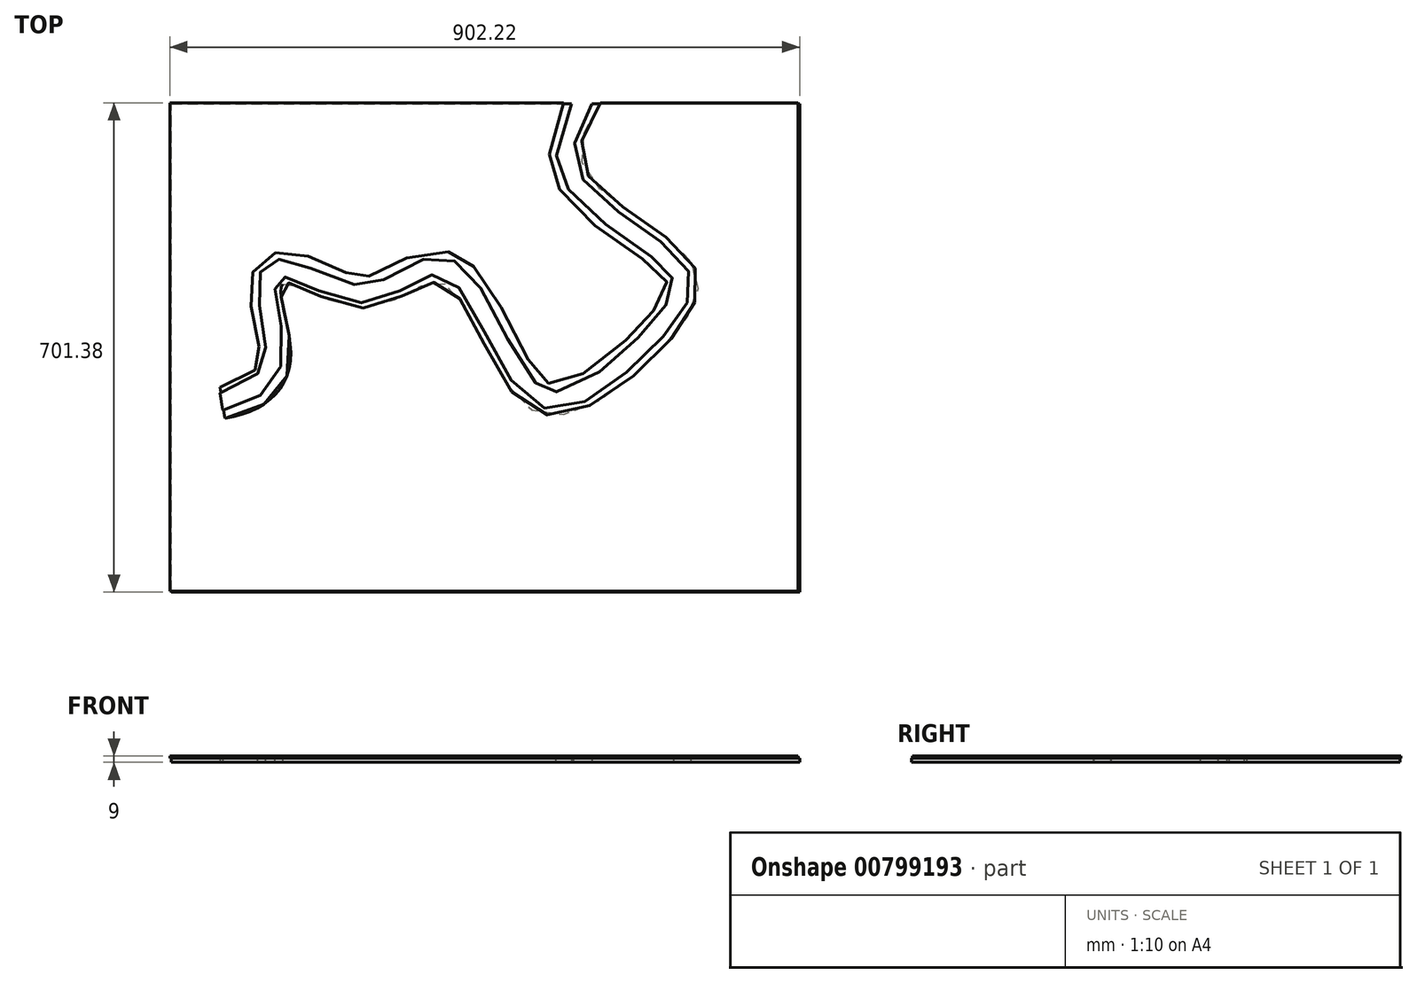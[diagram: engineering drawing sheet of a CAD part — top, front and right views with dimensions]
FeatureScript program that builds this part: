
annotation { "Feature Type Name" : "Feature", "Feature Type Description" : "" }
export const myFeature = defineFeature(function(context is Context, id is Id, definition is map)
    precondition{}
    {
        {
            var Q0;
            Q0=qCreatedBy(makeId("Top.planeOp"),FACE);
            var sketch = newSketch(context, id + "F0", { "sketchPlane" : qUnion([Q0])});
            skLineSegment(sketch, "E0.bottom", {"start": v(-313.22, -209.62) * mm, "end": v(586.78, -209.62) * mm});
            skLineSegment(sketch, "E0.top", {"start": v(-313.22, 490.38) * mm, "end": v(586.78, 490.38) * mm});
            skLineSegment(sketch, "E0.left", {"start": v(-313.22, -209.62) * mm, "end": v(-313.22, 490.38) * mm});
            skLineSegment(sketch, "E0.right", {"start": v(586.78, -209.62) * mm, "end": v(586.78, 490.38) * mm});
            skSolve(sketch);
        }
        {
            var Q0;
            Q0=qCreatedBy(makeId("Top.planeOp"),FACE);
            var sketch = newSketch(context, id + "F1", { "sketchPlane" : qUnion([Q0])});
            skFitSpline(sketch, "E1", {"points": [v(-234.3, 37.79) * mm, v(-140.37, 121) * mm, v(-151.1, 231.03) * mm, v(-33, 196.14) * mm, v(79.72, 231.03) * mm, v(203.18, 51.2) * mm, v(383, 129.04) * mm, v(436.68, 257.87) * mm, v(281.01, 394.76) * mm, v(345.43, 545.06) * mm], "startDerivative": vector(1524.68, 246.4) * mm, "endDerivative": vector(1140, 1409.82) * mm});
            skFitSpline(sketch, "E2.0", {"points": [v(-241.49, 82.21) * mm, v(-235.54, 83.17) * mm, v(-227.18, 85.14) * mm, v(-217.47, 88.6) * mm, v(-210.97, 91.54) * mm, v(-205.27, 94.74) * mm, v(-200.42, 98.12) * mm, v(-196.37, 101.6) * mm, v(-193.1, 105.12) * mm, v(-190.48, 108.67) * mm, v(-188.77, 111.71) * mm, v(-187.64, 114.26) * mm, v(-186.91, 116.25) * mm, v(-186.29, 118.34) * mm, v(-185.86, 120.2) * mm, v(-185.58, 121.76) * mm, v(-185.4, 122.98) * mm, v(-185.25, 124.24) * mm, v(-185.14, 125.55) * mm, v(-185.06, 127) * mm, v(-185, 129.09) * mm, v(-185.02, 131.99) * mm, v(-185.23, 135.87) * mm, v(-185.6, 140.08) * mm, v(-186.16, 144.57) * mm, v(-187.1, 150.85) * mm, v(-188.62, 159.15) * mm, v(-190.82, 169.5) * mm, v(-192.8, 178.27) * mm, v(-194.38, 185.3) * mm, v(-195.53, 190.6) * mm, v(-196.61, 195.94) * mm, v(-197.6, 201.35) * mm, v(-198.47, 206.9) * mm, v(-199.15, 212.74) * mm, v(-199.48, 218.02) * mm, v(-199.49, 222.66) * mm, v(-199.33, 226.42) * mm, v(-198.92, 230.53) * mm, v(-198.17, 235.06) * mm, v(-196.91, 240.08) * mm, v(-194.95, 245.63) * mm, v(-192.49, 250.64) * mm, v(-189.9, 254.77) * mm, v(-187.62, 257.88) * mm, v(-185, 260.93) * mm, v(-182.04, 263.87) * mm, v(-179.31, 266.15) * mm, v(-177, 267.85) * mm, v(-174.62, 269.45) * mm, v(-171.6, 271.2) * mm, v(-167.98, 272.95) * mm, v(-164.4, 274.33) * mm, v(-159.8, 275.75) * mm, v(-154.43, 276.82) * mm, v(-148.71, 277.31) * mm, v(-143.68, 277.28) * mm, v(-139.23, 276.9) * mm, v(-135.25, 276.33) * mm, v(-131.65, 275.6) * mm, v(-128.33, 274.8) * mm, v(-124.2, 273.62) * mm, v(-119.45, 272.03) * mm, v(-114.13, 270) * mm, v(-109.02, 267.87) * mm, v(-104, 265.67) * mm, v(-99.04, 263.41) * mm, v(-94.1, 261.12) * mm, v(-87.5, 258.07) * mm, v(-79.29, 254.3) * mm, v(-69.56, 250.1) * mm, v(-61.74, 247.1) * mm, v(-55.8, 245.08) * mm, v(-51.55, 243.8) * mm, v(-47.55, 242.76) * mm, v(-43.86, 241.98) * mm, v(-41.09, 241.53) * mm, v(-39.08, 241.3) * mm, v(-37.68, 241.18) * mm, v(-36.4, 241.12) * mm, v(-35.42, 241.1) * mm, v(-34.7, 241.11) * mm, v(-34.2, 241.13) * mm, v(-33.69, 241.15) * mm, v(-32.98, 241.2) * mm, v(-32.08, 241.3) * mm, v(-30.94, 241.45) * mm, v(-29.75, 241.65) * mm, v(-28.07, 242) * mm, v(-25.82, 242.56) * mm, v(-21.88, 243.8) * mm, v(-16.33, 245.98) * mm, v(-8.81, 249.56) * mm, v(-0.54, 253.95) * mm, v(8.45, 258.93) * mm, v(16.64, 263.34) * mm, v(23.76, 266.88) * mm, v(29.45, 269.5) * mm, v(35.56, 272) * mm, v(42.18, 274.31) * mm, v(49.42, 276.3) * mm, v(57.37, 277.8) * mm, v(66.05, 278.55) * mm, v(75.38, 278.28) * mm, v(83.51, 276.98) * mm, v(89.2, 275.43) * mm, v(92.44, 274.37) * mm, v(94.84, 273.49) * mm, v(96.82, 272.68) * mm, v(98.38, 271.98) * mm, v(99.93, 271.27) * mm, v(101.8, 270.35) * mm, v(104.7, 268.8) * mm, v(108.13, 266.74) * mm, v(111.95, 264.14) * mm, v(115.5, 261.43) * mm, v(119.93, 257.72) * mm, v(124.92, 252.93) * mm, v(130.25, 247.03) * mm, v(135.09, 241) * mm, v(139.55, 234.84) * mm, v(145.13, 226.49) * mm, v(151.56, 215.76) * mm, v(158.77, 202.5) * mm, v(165.68, 188.95) * mm, v(172.42, 175.3) * mm, v(179.06, 161.74) * mm, v(185.66, 148.52) * mm, v(192.24, 135.9) * mm, v(198.8, 124.17) * mm, v(205.28, 113.64) * mm, v(210.51, 106.14) * mm, v(214.49, 101.06) * mm, v(217.33, 97.75) * mm, v(219.98, 94.97) * mm, v(222.38, 92.74) * mm, v(224.11, 91.33) * mm, v(225.31, 90.46) * mm, v(226.12, 89.92) * mm, v(226.8, 89.5) * mm, v(227.47, 89.14) * mm, v(228.13, 88.82) * mm, v(229, 88.44) * mm, v(230.1, 88.05) * mm, v(231.55, 87.67) * mm, v(233.18, 87.38) * mm, v(235.06, 87.2) * mm, v(237.23, 87.16) * mm, v(240.56, 87.34) * mm, v(245.52, 88.08) * mm, v(252.68, 90) * mm, v(260.83, 93.03) * mm, v(269.76, 97.18) * mm, v(279.26, 102.4) * mm, v(289.15, 108.58) * mm, v(299.28, 115.62) * mm, v(309.5, 123.37) * mm, v(319.73, 131.71) * mm, v(329.83, 140.5) * mm, v(338.06, 148.1) * mm, v(344.5, 154.26) * mm, v(348.45, 158.13) * mm, v(351.56, 161.24) * mm, v(354.63, 164.33) * mm, v(358.35, 168.16) * mm, v(362.65, 172.7) * mm, v(368.12, 178.65) * mm, v(374.44, 185.9) * mm, v(381.12, 194.2) * mm, v(386.79, 202.03) * mm, v(391.37, 209.25) * mm, v(394.83, 215.7) * mm, v(397.17, 221.22) * mm, v(398.27, 224.9) * mm, v(398.76, 227.25) * mm, v(398.96, 228.73) * mm, v(399.03, 229.95) * mm, v(399.02, 230.95) * mm, v(398.94, 231.79) * mm, v(398.8, 232.54) * mm, v(398.6, 233.28) * mm, v(398.36, 233.97) * mm, v(398.1, 234.6) * mm, v(397.89, 235.03) * mm, v(397.7, 235.4) * mm, v(397.54, 235.68) * mm, v(397.36, 236) * mm, v(397.09, 236.45) * mm, v(396.68, 237.09) * mm, v(395.87, 238.27) * mm, v(394.57, 240) * mm, v(392.51, 242.4) * mm, v(389.14, 246) * mm, v(383.77, 251.06) * mm, v(375.75, 257.74) * mm, v(366.42, 264.84) * mm, v(356.04, 272.25) * mm, v(344.87, 279.92) * mm, v(333.15, 287.84) * mm, v(321.1, 296.03) * mm, v(308.9, 304.53) * mm, v(296.74, 313.4) * mm, v(284.8, 322.77) * mm, v(273.24, 332.8) * mm, v(264.04, 341.9) * mm, v(257.06, 349.83) * mm, v(252.04, 356.16) * mm, v(248.1, 361.8) * mm, v(245.13, 366.57) * mm, v(243, 370.28) * mm, v(241.31, 373.49) * mm, v(240.03, 376.13) * mm, v(238.81, 378.8) * mm, v(237.4, 382.16) * mm, v(235.37, 387.62) * mm, v(233.3, 394.55) * mm, v(231.55, 402.95) * mm, v(230.52, 411.32) * mm, v(230.17, 419.6) * mm, v(230.45, 427.73) * mm, v(231.56, 438.3) * mm, v(234.19, 450.95) * mm, v(238.83, 465.24) * mm, v(244.61, 478.77) * mm, v(251.28, 491.68) * mm, v(258.65, 504.13) * mm, v(266.58, 516.22) * mm, v(274.94, 528.03) * mm, v(283.61, 539.62) * mm, v(295.46, 554.84) * mm, v(304.5, 566) * mm, v(310.44, 573.35) * mm]});
            skLineSegment(sketch, "E3", {"start": v(-241.49, 82.21) * mm, "end": v(-234.3, 37.79) * mm});
            skLineSegment(sketch, "E4", {"start": v(345.43, 545.06) * mm, "end": v(310.44, 573.35) * mm});
            skSolve(sketch);
        }
        {
            var Q0;
            Q0=qSketchRegion(id+"F0",true);
            extrude(context, id + "F2", {"entities" : qUnion([Q0]), "depth" : 3 * mm, "offsetDistance" : 25 * mm});
        }
        {
            var Q0;
            Q0=qSketchRegion(id+"F1",true);
            extrude(context, id + "F3", {"entities" : qUnion([Q0]), "operationType" : NewBodyOperationType.REMOVE, "depth" : 25 * mm, "offsetDistance" : 25 * mm, "hasSecondDirection" : true, "secondDirectionOppositeDirection" : true, "secondDirectionDepth" : 25 * mm});
        }
        {
            var Q0;
            Q0=qCreatedBy(makeId("Top.planeOp"),FACE);
            var sketch = newSketch(context, id + "F4", { "sketchPlane" : qUnion([Q0])});
            skFitSpline(sketch, "E5", {"points": [v(-329.28, -233.28) * mm, v(-243.32, -152.04) * mm, v(-250.13, -43.12) * mm, v(-125.32, -79.42) * mm, v(-10.38, -40.77) * mm, v(117.48, -224.65) * mm, v(288.03, -142.03) * mm, v(335.32, -29.5) * mm, v(179.23, 110.07) * mm, v(250.45, 273.99) * mm], "startDerivative": vector(1524.68, 246.4) * mm, "endDerivative": vector(1140, 1409.82) * mm});
            skFitSpline(sketch, "E6.0", {"points": [v(-333.27, -208.6) * mm, v(-326.54, -207.51) * mm, v(-317.2, -205.24) * mm, v(-306.38, -201.13) * mm, v(-299.12, -197.57) * mm, v(-292.69, -193.58) * mm, v(-287.08, -189.2) * mm, v(-282.25, -184.47) * mm, v(-278.16, -179.38) * mm, v(-274.75, -173.88) * mm, v(-272, -167.9) * mm, v(-270.26, -162.45) * mm, v(-269.35, -158.34) * mm, v(-268.92, -155.91) * mm, v(-268.64, -154.04) * mm, v(-268.42, -152.13) * mm, v(-268.27, -150.5) * mm, v(-268.18, -149.16) * mm, v(-268.1, -147.79) * mm, v(-268.04, -146.03) * mm, v(-268, -143.84) * mm, v(-268.03, -140.83) * mm, v(-268.18, -136.9) * mm, v(-268.54, -131.97) * mm, v(-269.24, -125.18) * mm, v(-270.46, -116.36) * mm, v(-272.3, -105.55) * mm, v(-274.33, -94.74) * mm, v(-276.32, -84.13) * mm, v(-277.77, -75.54) * mm, v(-278.7, -68.8) * mm, v(-279.22, -63.78) * mm, v(-279.54, -58.73) * mm, v(-279.56, -53.56) * mm, v(-279.23, -49.02) * mm, v(-278.6, -45.13) * mm, v(-277.9, -42.06) * mm, v(-276.88, -38.81) * mm, v(-275.45, -35.39) * mm, v(-273.48, -31.84) * mm, v(-271.3, -28.87) * mm, v(-269.22, -26.58) * mm, v(-267.5, -24.94) * mm, v(-265.93, -23.67) * mm, v(-264.6, -22.72) * mm, v(-263.58, -22.04) * mm, v(-262.54, -21.4) * mm, v(-261.14, -20.62) * mm, v(-259.37, -19.76) * mm, v(-257.27, -18.92) * mm, v(-254.5, -18.02) * mm, v(-251.2, -17.3) * mm, v(-247.53, -16.9) * mm, v(-244.15, -16.83) * mm, v(-241.02, -17) * mm, v(-238.1, -17.36) * mm, v(-234.43, -18) * mm, v(-230.15, -19.07) * mm, v(-225.24, -20.6) * mm, v(-220.43, -22.37) * mm, v(-215.62, -24.3) * mm, v(-209.16, -27.07) * mm, v(-200.92, -30.82) * mm, v(-190.7, -35.56) * mm, v(-180.25, -40.28) * mm, v(-169.7, -44.71) * mm, v(-159.26, -48.6) * mm, v(-150.83, -51.16) * mm, v(-144.4, -52.7) * mm, v(-139.76, -53.6) * mm, v(-135.35, -54.2) * mm, v(-131.9, -54.46) * mm, v(-129.28, -54.53) * mm, v(-127.39, -54.5) * mm, v(-125.58, -54.4) * mm, v(-123.76, -54.24) * mm, v(-121.92, -54) * mm, v(-119.44, -53.6) * mm, v(-115.02, -52.63) * mm, v(-108.46, -50.55) * mm, v(-100.2, -47.01) * mm, v(-91.65, -42.63) * mm, v(-82.84, -37.63) * mm, v(-73.78, -32.3) * mm, v(-64.42, -26.92) * mm, v(-56.22, -22.65) * mm, v(-49.28, -19.55) * mm, v(-43.81, -17.45) * mm, v(-38.04, -15.66) * mm, v(-31.91, -14.28) * mm, v(-25.39, -13.48) * mm, v(-18.5, -13.42) * mm, v(-12.56, -14.13) * mm, v(-7.79, -15.23) * mm, v(-4.82, -16.13) * mm, v(-2.48, -16.98) * mm, v(-0.74, -17.69) * mm, v(0.97, -18.46) * mm, v(3.19, -19.54) * mm, v(5.85, -21.01) * mm, v(9.87, -23.56) * mm, v(14.5, -27.07) * mm, v(19.54, -31.66) * mm, v(24.17, -36.56) * mm, v(28.5, -41.75) * mm, v(32.61, -47.19) * mm, v(37.85, -54.76) * mm, v(44.07, -64.8) * mm, v(51.22, -77.59) * mm, v(58.2, -90.95) * mm, v(65.1, -104.67) * mm, v(71.98, -118.53) * mm, v(78.9, -132.26) * mm, v(85.86, -145.61) * mm, v(92.9, -158.3) * mm, v(100, -170.04) * mm, v(107.11, -180.53) * mm, v(112.99, -187.97) * mm, v(117.56, -193) * mm, v(120.9, -196.27) * mm, v(123.56, -198.58) * mm, v(125.61, -200.17) * mm, v(127.1, -201.23) * mm, v(128.3, -202.01) * mm, v(129.23, -202.58) * mm, v(130.14, -203.1) * mm, v(131.27, -203.7) * mm, v(132.63, -204.33) * mm, v(133.99, -204.9) * mm, v(135.82, -205.55) * mm, v(138.15, -206.2) * mm, v(141.08, -206.74) * mm, v(145.21, -207.13) * mm, v(150.9, -206.98) * mm, v(158.66, -205.64) * mm, v(167.24, -203.07) * mm, v(176.5, -199.26) * mm, v(186.27, -194.27) * mm, v(196.38, -188.2) * mm, v(206.71, -181.2) * mm, v(217.13, -173.38) * mm, v(227.54, -164.92) * mm, v(237.85, -155.95) * mm, v(247.97, -146.62) * mm, v(256.18, -138.68) * mm, v(262.58, -132.3) * mm, v(267.29, -127.51) * mm, v(271.9, -122.75) * mm, v(276.35, -118.06) * mm, v(280.64, -113.46) * mm, v(286.1, -107.43) * mm, v(292.45, -100.11) * mm, v(299.17, -91.72) * mm, v(304.9, -83.77) * mm, v(309.53, -76.35) * mm, v(313.03, -69.56) * mm, v(315.38, -63.52) * mm, v(316.45, -59.18) * mm, v(316.87, -56.11) * mm, v(316.98, -53.98) * mm, v(316.92, -51.98) * mm, v(316.69, -50.07) * mm, v(316.28, -48.17) * mm, v(315.78, -46.54) * mm, v(315.25, -45.2) * mm, v(314.8, -44.15) * mm, v(314.35, -43.25) * mm, v(313.96, -42.51) * mm, v(313.64, -41.95) * mm, v(313.3, -41.37) * mm, v(312.8, -40.57) * mm, v(312.12, -39.52) * mm, v(311.18, -38.19) * mm, v(309.78, -36.33) * mm, v(307.74, -33.87) * mm, v(304.84, -30.72) * mm, v(301.53, -27.42) * mm, v(296.58, -22.85) * mm, v(289.5, -16.9) * mm, v(279.83, -9.45) * mm, v(269.23, -1.78) * mm, v(257.93, 6.1) * mm, v(246.18, 14.16) * mm, v(234.19, 22.45) * mm, v(222.16, 30.97) * mm, v(210.3, 39.77) * mm, v(198.81, 48.92) * mm, v(187.87, 58.5) * mm, v(179.37, 66.95) * mm, v(173.05, 74.08) * mm, v(168.58, 79.64) * mm, v(164.41, 85.45) * mm, v(161.24, 90.51) * mm, v(158.9, 94.72) * mm, v(157.27, 97.96) * mm, v(155.76, 101.28) * mm, v(154.4, 104.64) * mm, v(153.17, 108.03) * mm, v(151.74, 112.58) * mm, v(149.76, 120.63) * mm, v(148.36, 132.2) * mm, v(148.77, 145.9) * mm, v(150.94, 159.27) * mm, v(154.56, 172.24) * mm, v(159.38, 184.86) * mm, v(165.2, 197.18) * mm, v(171.86, 209.28) * mm, v(181.66, 225.16) * mm, v(195.32, 244.62) * mm, v(213.03, 267.48) * mm, v(225.08, 282.37) * mm, v(231.01, 289.7) * mm]});
            skLineSegment(sketch, "E7", {"start": v(-333.27, -208.6) * mm, "end": v(-329.28, -233.28) * mm});
            skLineSegment(sketch, "E8", {"start": v(250.45, 273.99) * mm, "end": v(231.01, 289.7) * mm});
            skSolve(sketch);
        }
        {
            var Q0;
            Q0=makeQuery(id+"F2.opExtrude","SWEPT_BODY",BODY,{"disambiguationData":[OSD([sQuery(id+"F0.wireOp",EDGE,"E0.bottom"),sQuery(id+"F0.wireOp",EDGE,"E0.top"),sQuery(id+"F0.wireOp",EDGE,"E0.left"),sQuery(id+"F0.wireOp",EDGE,"E0.right")])]});
            transform(context, id + "F5", {"entities" : qUnion([Q0]), "transformType" : TransformType.TRANSLATION_3D, "dx" : -139 * mm, "dy" : -139 * mm, "dz" : 6 * mm, "makeCopy" : false});
        }
        {
            var Q0;
            Q0=qSketchRegion(id+"F4",true);
            extrude(context, id + "F6", {"entities" : qUnion([Q0]), "depth" : 25 * mm, "offsetDistance" : 25 * mm, "hasSecondDirection" : true, "secondDirectionOppositeDirection" : true, "secondDirectionDepth" : 25 * mm});
        }
        {
            var Q0;
            Q0=qCreatedBy(makeId("Top.planeOp"),FACE);
            var sketch = newSketch(context, id + "F7", { "sketchPlane" : qUnion([Q0])});
            skLineSegment(sketch, "E9.bottom", {"start": v(-450, -350) * mm, "end": v(450, -350) * mm});
            skLineSegment(sketch, "E9.top", {"start": v(-450, 350) * mm, "end": v(450, 350) * mm});
            skLineSegment(sketch, "E9.left", {"start": v(-450, -350) * mm, "end": v(-450, 350) * mm});
            skLineSegment(sketch, "E9.right", {"start": v(450, -350) * mm, "end": v(450, 350) * mm});
            skSolve(sketch);
        }
        {
            var Q0;
            Q0=makeQuery(id+"F6.opExtrude","SWEPT_BODY",BODY,{"disambiguationData":[OSD([sQuery(id+"F4.wireOp",EDGE,"E5"),sQuery(id+"F4.wireOp",EDGE,"E6.0"),sQuery(id+"F4.wireOp",EDGE,"E7"),sQuery(id+"F4.wireOp",EDGE,"E8")])]});
            transform(context, id + "F8", {"entities" : qUnion([Q0]), "transformType" : TransformType.TRANSLATION_3D, "dx" : -47 * mm, "dy" : 144 * mm, "dz" : 0 * mm, "makeCopy" : false});
        }
        {
            var Q0;
            Q0=qSketchRegion(id+"F7",true);
            extrude(context, id + "F9", {"entities" : qUnion([Q0]), "depth" : 6 * mm, "offsetDistance" : 25 * mm});
        }
        {
            var Q0;
            Q0=makeQuery(id+"F6.opExtrude","SWEPT_BODY",BODY,{"disambiguationData":[OSD([sQuery(id+"F4.wireOp",EDGE,"E5"),sQuery(id+"F4.wireOp",EDGE,"E6.0"),sQuery(id+"F4.wireOp",EDGE,"E7"),sQuery(id+"F4.wireOp",EDGE,"E8")])]});
            var Q1;
            Q1=makeQuery(id+"F2.opExtrude","SWEPT_BODY",BODY,{"disambiguationData":[OSD([sQuery(id+"F0.wireOp",EDGE,"E0.bottom"),sQuery(id+"F0.wireOp",EDGE,"E0.top"),sQuery(id+"F0.wireOp",EDGE,"E0.left"),sQuery(id+"F0.wireOp",EDGE,"E0.right")])]});
            var Q2;
            Q2=makeQuery(id+"F9.opExtrude","SWEPT_BODY",BODY,{"disambiguationData":[OSD([sQuery(id+"F7.wireOp",EDGE,"E9.bottom"),sQuery(id+"F7.wireOp",EDGE,"E9.top"),sQuery(id+"F7.wireOp",EDGE,"E9.left"),sQuery(id+"F7.wireOp",EDGE,"E9.right")])]});
            booleanBodies(context, id + "F10", {"operationType" : BooleanOperationType.SUBTRACTION, "tools" : qUnion([Q0]), "targets" : qUnion([Q1, Q2])});
        }
    });
